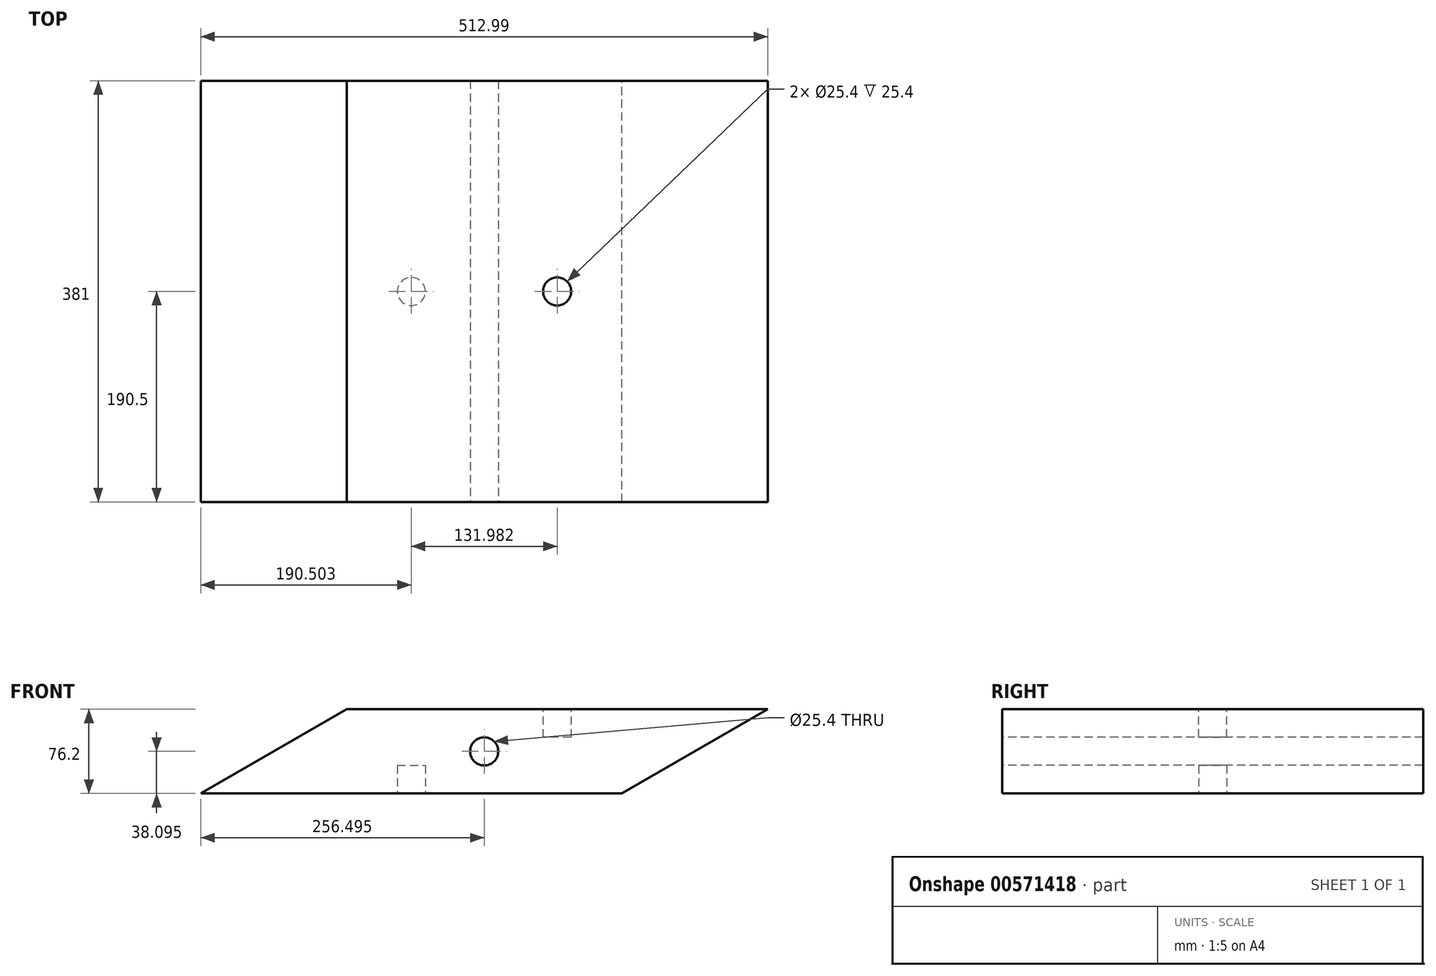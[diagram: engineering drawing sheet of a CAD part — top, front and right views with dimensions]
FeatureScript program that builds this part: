
annotation { "Feature Type Name" : "Feature", "Feature Type Description" : "" }
export const myFeature = defineFeature(function(context is Context, id is Id, definition is map)
    precondition{}
    {
        {
            var Q0;
            Q0=qCreatedBy(makeId("Front.planeOp"),FACE);
            var sketch = newSketch(context, id + "F0", { "sketchPlane" : qUnion([Q0])});
            skLineSegment(sketch, "E0", {"start": v(-231.23, -55.03) * mm, "end": v(149.77, -55.03) * mm});
            skLineSegment(sketch, "E1", {"start": v(149.77, -55.03) * mm, "end": v(281.76, 21.17) * mm});
            skLineSegment(sketch, "E2", {"start": v(281.76, 21.17) * mm, "end": v(-99.24, 21.17) * mm});
            skLineSegment(sketch, "E3", {"start": v(-99.24, 21.17) * mm, "end": v(-231.23, -55.03) * mm});
            skSolve(sketch);
        }
        {
            var Q0;
            Q0=makeQuery(id+"F0.imprint","IMPRINT",FACE,{"disambiguationData":[TD([[makeQuery(id+"F0.imprint","IMPRINT",EDGE,{"derivedFrom":sQuery(id+"F0.wireOp",EDGE,"E0")}),1.0]])]});
            extrude(context, id + "F1", {"entities" : qUnion([Q0]), "depth" : 381 * mm, "offsetDistance" : 25.4 * mm});
        }
        {
            var Q0;
            Q0=makeQuery(id+"F1.opExtrude","CAP_FACE",FACE,{"disambiguationData":[OSD([sQuery(id+"F0.wireOp",EDGE,"E0"),sQuery(id+"F0.wireOp",EDGE,"E1"),sQuery(id+"F0.wireOp",EDGE,"E2"),sQuery(id+"F0.wireOp",EDGE,"E3")])],"isStart":false});
            var sketch = newSketch(context, id + "F2", { "sketchPlane" : qUnion([Q0])});
            skLineSegment(sketch, "E4", {"start": v(91.26, 21.17) * mm, "end": v(-40.73, -55.03) * mm, "construction": true});
            skLineSegment(sketch, "E5", {"start": v(-165.24, -16.93) * mm, "end": v(215.76, -16.93) * mm, "construction": true});
            skCircle(sketch, "E6", {"center": v(25.26, -16.93) * mm, "radius": 12.7 * mm});
            skSolve(sketch);
        }
        {
            var Q0;
            Q0=makeQuery(id+"F2.imprint","IMPRINT",FACE,{"disambiguationData":[TD([[makeQuery(id+"F2.imprint","IMPRINT",EDGE,{"derivedFrom":sQuery(id+"F2.wireOp",EDGE,"E6")}),1.0]])]});
            extrude(context, id + "F3", {"entities" : qUnion([Q0]), "operationType" : NewBodyOperationType.REMOVE, "oppositeDirection" : true, "depth" : 381 * mm, "offsetDistance" : 25.4 * mm});
        }
        {
            var Q0;
            Q0=makeQuery(id+"F1.opExtrude","SWEPT_FACE",FACE,{"disambiguationData":[OSD([sQuery(id+"F0.wireOp",EDGE,"E2")])]});
            var sketch = newSketch(context, id + "F4", { "sketchPlane" : qUnion([Q0])});
            skLineSegment(sketch, "E7", {"start": v(91.26, 0) * mm, "end": v(91.26, -381) * mm, "construction": true});
            skLineSegment(sketch, "E8", {"start": v(-99.24, -190.5) * mm, "end": v(281.76, -190.5) * mm, "construction": true});
            skCircle(sketch, "E9", {"center": v(91.26, -190.5) * mm, "radius": 12.7 * mm});
            skSolve(sketch);
        }
        {
            var Q0;
            Q0=makeQuery(id+"F1.opExtrude","SWEPT_FACE",FACE,{"disambiguationData":[OSD([sQuery(id+"F0.wireOp",EDGE,"E0")])]});
            var sketch = newSketch(context, id + "F5", { "sketchPlane" : qUnion([Q0])});
            skLineSegment(sketch, "E10", {"start": v(-231.23, 190.5) * mm, "end": v(149.77, 190.5) * mm, "construction": true});
            skLineSegment(sketch, "E11", {"start": v(-40.73, 381) * mm, "end": v(-40.73, 0) * mm, "construction": true});
            skCircle(sketch, "E12", {"center": v(-40.73, 190.5) * mm, "radius": 12.7 * mm});
            skSolve(sketch);
        }
        {
            var Q0;
            Q0 = qSketchRegion(id + "F5", true);
            extrude(context, id + "F6", {"entities" : qUnion([Q0]), "operationType" : NewBodyOperationType.REMOVE, "oppositeDirection" : true, "depth" : 25.4 * mm, "offsetDistance" : 25.4 * mm});
        }
        {
            var Q0;
            Q0=makeQuery(id+"F4.imprint","IMPRINT",FACE,{"disambiguationData":[TD([[makeQuery(id+"F4.imprint","IMPRINT",EDGE,{"derivedFrom":sQuery(id+"F4.wireOp",EDGE,"E9")}),1.0]])]});
            extrude(context, id + "F7", {"entities" : qUnion([Q0]), "operationType" : NewBodyOperationType.REMOVE, "oppositeDirection" : true, "depth" : 25.4 * mm, "offsetDistance" : 25.4 * mm});
        }
    });
